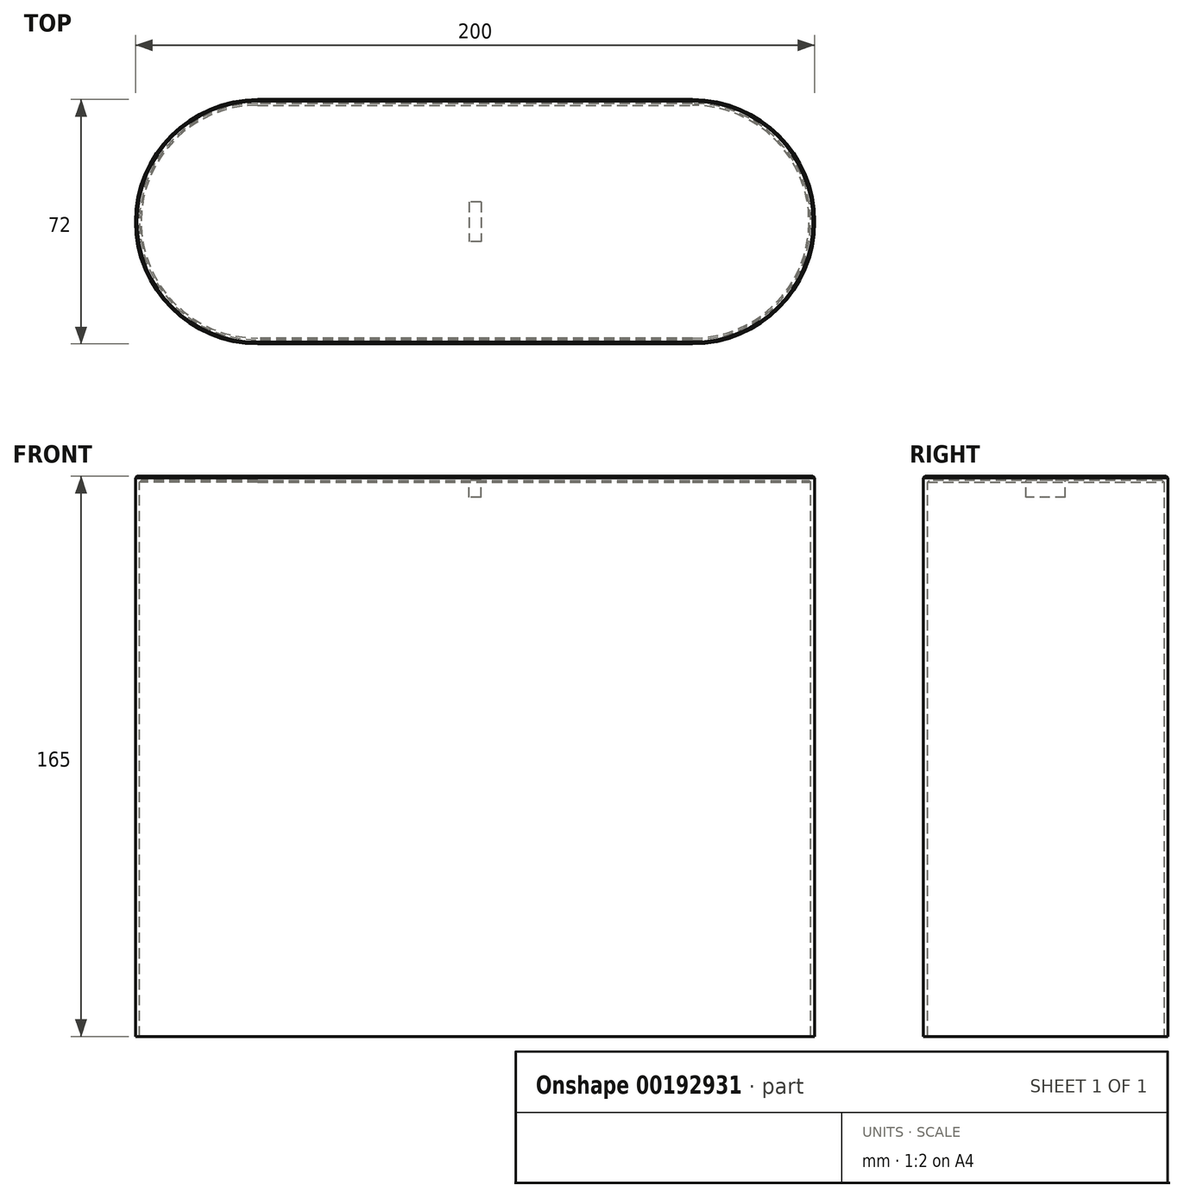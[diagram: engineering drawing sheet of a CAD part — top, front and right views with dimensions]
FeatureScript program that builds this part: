
annotation { "Feature Type Name" : "Feature", "Feature Type Description" : "" }
export const myFeature = defineFeature(function(context is Context, id is Id, definition is map)
    precondition{}
    {
        {
            var Q0;
            Q0=qCreatedBy(makeId("Top.planeOp"),FACE);
            var sketch = newSketch(context, id + "F0", { "sketchPlane" : qUnion([Q0])});
            skLineSegment(sketch, "E0.bottom", {"start": v(64, -36) * mm, "end": v(-64, -36) * mm});
            skLineSegment(sketch, "E0.top", {"start": v(64, 36) * mm, "end": v(-64, 36) * mm});
            skLineSegment(sketch, "E0.left", {"start": v(100, 0) * mm, "end": v(100, 0) * mm});
            skLineSegment(sketch, "E0.right", {"start": v(-100, 0) * mm, "end": v(-100, 0) * mm});
            skPoint(sketch, "E0.middle", {"position": v(0, 0) * mm});
            skPoint(sketch, "E1.visualSharp", {"position": v(-100, 36) * mm});
            skArc(sketch, "E1.filletArc", {"start": v(-64, 36) * mm, "mid": v(-89.46, 25.46) * mm, "end": v(-100, 0) * mm});
            skPoint(sketch, "E2.visualSharp", {"position": v(-100, -36) * mm});
            skArc(sketch, "E2.filletArc", {"start": v(-100, 0) * mm, "mid": v(-89.46, -25.46) * mm, "end": v(-64, -36) * mm});
            skPoint(sketch, "E3.visualSharp", {"position": v(100, 36) * mm});
            skArc(sketch, "E3.filletArc", {"start": v(100, 0) * mm, "mid": v(89.46, 25.46) * mm, "end": v(64, 36) * mm});
            skPoint(sketch, "E4.visualSharp", {"position": v(100, -36) * mm});
            skArc(sketch, "E4.filletArc", {"start": v(64, -36) * mm, "mid": v(89.46, -25.46) * mm, "end": v(100, 0) * mm});
            skSolve(sketch);
        }
        {
            var Q0;
            Q0=qCreatedBy(makeId("Top.planeOp"),FACE);
            cPlane(context, id + "F1", {"entities" : qUnion([Q0]), "cplaneType" : CPlaneType.OFFSET, "offset" : 165 * mm, "width" : 150 * mm, "height" : 150 * mm});
        }
        {
            var Q0;
            Q0=qCreatedBy(id+"F1.planeOp",FACE);
            var sketch = newSketch(context, id + "F2", { "sketchPlane" : qUnion([Q0])});
            skLineSegment(sketch, "E5.bottom", {"start": v(64, -36) * mm, "end": v(-64, -36) * mm});
            skLineSegment(sketch, "E5.top", {"start": v(64, 36) * mm, "end": v(-64, 36) * mm});
            skLineSegment(sketch, "E5.left", {"start": v(100, 0) * mm, "end": v(100, 0) * mm});
            skLineSegment(sketch, "E5.right", {"start": v(-100, 0) * mm, "end": v(-100, 0) * mm});
            skPoint(sketch, "E5.middle", {"position": v(0, 0) * mm});
            skPoint(sketch, "E6.visualSharp", {"position": v(-100, 36) * mm});
            skArc(sketch, "E6.filletArc", {"start": v(-64, 36) * mm, "mid": v(-89.46, 25.46) * mm, "end": v(-100, 0) * mm});
            skPoint(sketch, "E7.visualSharp", {"position": v(-100, -36) * mm});
            skArc(sketch, "E7.filletArc", {"start": v(-100, 0) * mm, "mid": v(-89.46, -25.46) * mm, "end": v(-64, -36) * mm});
            skPoint(sketch, "E8.visualSharp", {"position": v(100, -36) * mm});
            skArc(sketch, "E8.filletArc", {"start": v(64, -36) * mm, "mid": v(89.46, -25.46) * mm, "end": v(100, 0) * mm});
            skPoint(sketch, "E9.visualSharp", {"position": v(100, 36) * mm});
            skArc(sketch, "E9.filletArc", {"start": v(100, 0) * mm, "mid": v(89.46, 25.46) * mm, "end": v(64, 36) * mm});
            skSolve(sketch);
        }
        {
            var Q0;
            Q0=makeQuery(id+"F2.imprint","IMPRINT",FACE,{"disambiguationData":[TD([[makeQuery(id+"F2.imprint","IMPRINT",EDGE,{"derivedFrom":sQuery(id+"F2.wireOp",EDGE,"E5.bottom")}),-1.0]])]});
            var Q1;
            Q1=makeQuery(id+"F0.imprint","IMPRINT",FACE,{"disambiguationData":[TD([[makeQuery(id+"F0.imprint","IMPRINT",EDGE,{"derivedFrom":sQuery(id+"F0.wireOp",EDGE,"E0.bottom")}),-1.0]])]});
            loft(context, id + "F3", {"sheetProfilesArray" : [{ "sheetProfileEntities" : qUnion([Q0]) }, { "sheetProfileEntities" : qUnion([Q1]) }]});
        }
        {
            var Q0;
            Q0=makeQuery(id+"F3.opLoft","CAP_FACE",FACE,{"disambiguationData":[OSD([makeQuery(id+"F0.imprint","IMPRINT",FACE,{"disambiguationData":[TD([[makeQuery(id+"F0.imprint","IMPRINT",EDGE,{"derivedFrom":sQuery(id+"F0.wireOp",EDGE,"E0.bottom")}),-1.0]])]})])],"isStart":true});
            shell(context, id + "F4", {"entities" : qUnion([Q0]), "thickness" : 1.2 * mm});
        }
        {
            var Q0;
            Q0=makeQuery(id+"F3.opLoft","MID_CAP_EDGE",EDGE,{"disambiguationData":[OSD([sQuery(id+"F2.wireOp",EDGE,"E5.bottom"),sQuery(id+"F2.wireOp",EDGE,"E6.filletArc"),sQuery(id+"F2.wireOp",EDGE,"E7.filletArc")])],"capPos":0.0});
            var Q1;
            Q1=makeQuery(id+"F4.opShell","OFFSET_EDGE",EDGE,{"disambiguationData":[OSD([sQuery(id+"F2.wireOp",EDGE,"E5.bottom"),sQuery(id+"F2.wireOp",EDGE,"E7.filletArc"),sQuery(id+"F2.wireOp",EDGE,"E8.filletArc")])]});
            chamfer(context, id + "F5", {"entities" : qUnion([Q0, Q1]), "width" : 0.5 * mm, "tangentPropagation" : true});
        }
        {
            var Q0;
            Q0=makeQuery(id+"F4.opShell","OFFSET_FACE",FACE,{"disambiguationData":[OSD([makeQuery(id+"F2.imprint","IMPRINT",FACE,{"disambiguationData":[TD([[makeQuery(id+"F2.imprint","IMPRINT",EDGE,{"derivedFrom":sQuery(id+"F2.wireOp",EDGE,"E5.bottom")}),-1.0]])]})])]});
            var sketch = newSketch(context, id + "F6", { "sketchPlane" : qUnion([Q0])});
            skLineSegment(sketch, "E10.bottom", {"start": v(1.8, -5.8) * mm, "end": v(-1.8, -5.8) * mm});
            skLineSegment(sketch, "E10.top", {"start": v(1.8, 5.8) * mm, "end": v(-1.8, 5.8) * mm});
            skLineSegment(sketch, "E10.left", {"start": v(1.8, -5.8) * mm, "end": v(1.8, 5.8) * mm});
            skLineSegment(sketch, "E10.right", {"start": v(-1.8, -5.8) * mm, "end": v(-1.8, 5.8) * mm});
            skPoint(sketch, "E10.middle", {"position": v(0, 0) * mm});
            skSolve(sketch);
        }
        {
            var Q0;
            Q0 = qSketchRegion(id + "F6", true);
            extrude(context, id + "F7", {"entities" : qUnion([Q0]), "operationType" : NewBodyOperationType.ADD, "depth" : 5 * mm});
        }
    });
